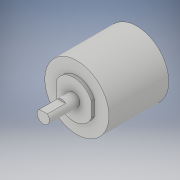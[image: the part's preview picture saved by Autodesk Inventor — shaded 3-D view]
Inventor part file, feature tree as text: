
AUTODESK INVENTOR PART (.ipt)
format: ipt  version: 2019 (Build 230136000, 136)  size: 131,584 bytes
history: native  units: mm
features: extrude x5, sketch x5, other x1
ambient origin geometry x8: Origin, YZ Plane, XZ Plane, XY Plane, X Axis, Y Axis, Z Axis, Center Point
bodies: Body1 (feature_tree)
feature tree (11):
  other  "ソリッド1"
  extrude  "押し出し1"  Depth=42.0mm
  extrude  "押し出し2"  Depth=39.2mm TaperAngle=0.0deg
  extrude  "押し出し3"  Depth=25.0mm
  extrude  "押し出し4"  Depth=2.0mm TaperAngle=0.0deg
  extrude  "押し出し5"  Depth=8.0mm
  sketch  "スケッチ1"
  sketch  "スケッチ2"
  sketch  "スケッチ3"
  sketch  "スケッチ4"
  sketch  "スケッチ5"
